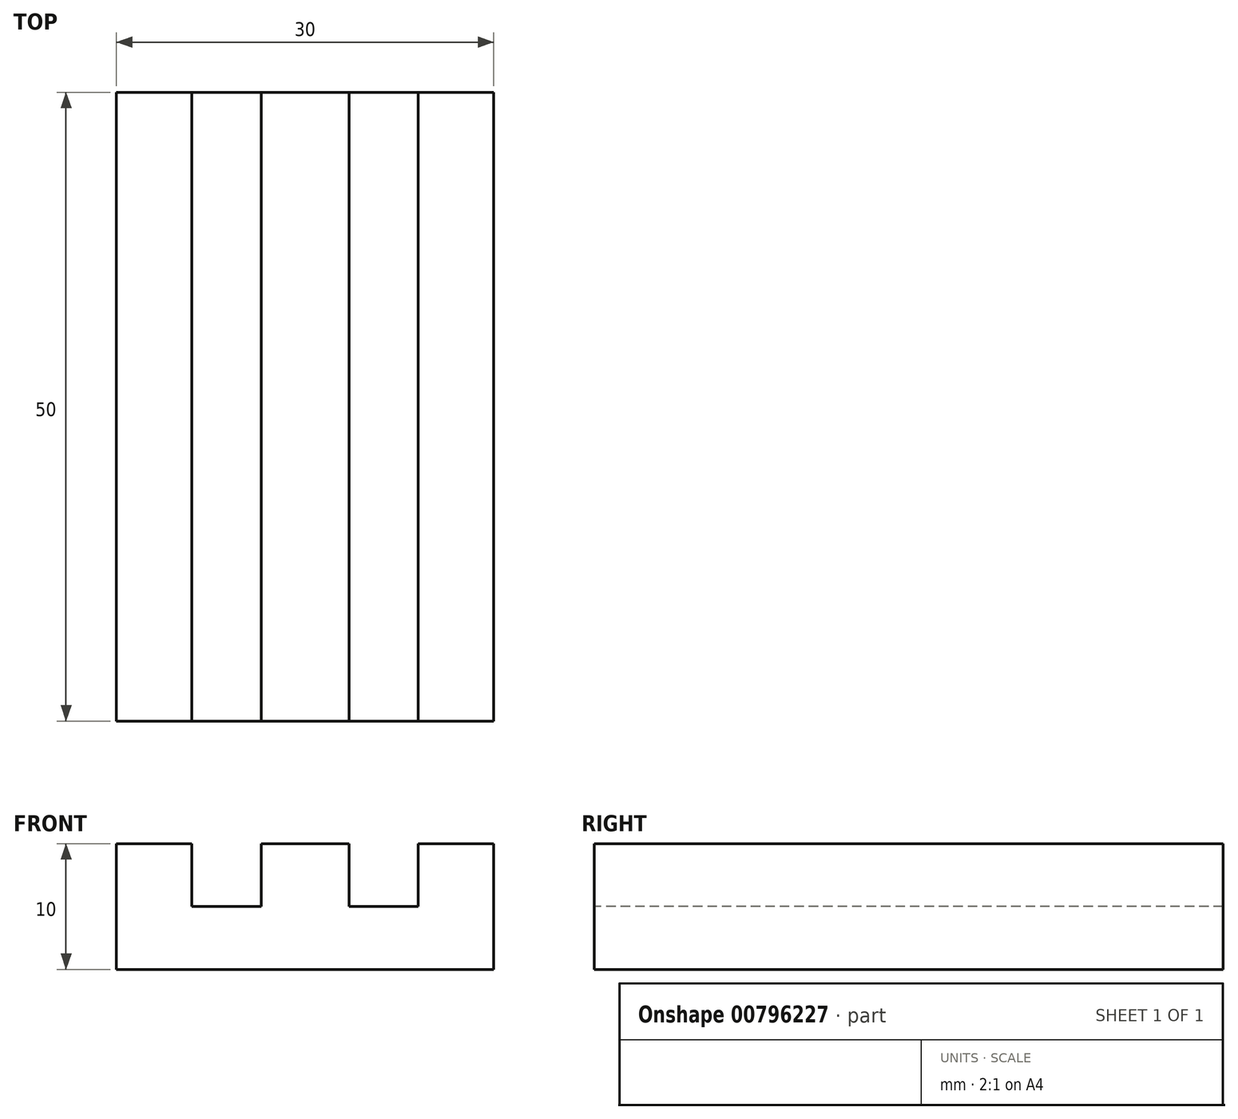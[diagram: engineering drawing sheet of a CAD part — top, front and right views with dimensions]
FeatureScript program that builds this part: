
annotation { "Feature Type Name" : "Feature", "Feature Type Description" : "" }
export const myFeature = defineFeature(function(context is Context, id is Id, definition is map)
    precondition{}
    {
        {
            var Q0;
            Q0=qCreatedBy(makeId("Top.planeOp"),FACE);
            var sketch = newSketch(context, id + "F0", { "sketchPlane" : qUnion([Q0])});
            skLineSegment(sketch, "E0", {"start": v(0, 0) * mm, "end": v(30, 0) * mm});
            skLineSegment(sketch, "E1", {"start": v(30, 0) * mm, "end": v(30, 50) * mm});
            skLineSegment(sketch, "E2", {"start": v(30, 50) * mm, "end": v(0, 50) * mm});
            skLineSegment(sketch, "E3", {"start": v(0, 50) * mm, "end": v(0, 0) * mm});
            skSolve(sketch);
        }
        {
            var Q0;
            Q0 = qSketchRegion(id + "F0", true);
            extrude(context, id + "F1", {"entities" : qUnion([Q0]), "depth" : 5 * mm, "offsetDistance" : 25 * mm});
        }
        {
            var Q0;
            Q0=makeQuery(id+"F1.opExtrude","CAP_FACE",FACE,{"disambiguationData":[OSD([sQuery(id+"F0.wireOp",EDGE,"E0"),sQuery(id+"F0.wireOp",EDGE,"E1"),sQuery(id+"F0.wireOp",EDGE,"E2"),sQuery(id+"F0.wireOp",EDGE,"E3")])],"isStart":false});
            var sketch = newSketch(context, id + "F2", { "sketchPlane" : qUnion([Q0])});
            skLineSegment(sketch, "E4", {"start": v(6, 0) * mm, "end": v(6, 50) * mm});
            skLineSegment(sketch, "E5", {"start": v(11.5, 50) * mm, "end": v(11.5, 0) * mm});
            skLineSegment(sketch, "E6", {"start": v(6, 50) * mm, "end": v(0, 50) * mm});
            skLineSegment(sketch, "E7", {"start": v(0, 50) * mm, "end": v(0, 0) * mm});
            skLineSegment(sketch, "E8", {"start": v(0, 0) * mm, "end": v(6, 0) * mm});
            skLineSegment(sketch, "E9", {"start": v(11.5, 0) * mm, "end": v(18.5, 0) * mm});
            skLineSegment(sketch, "E10", {"start": v(18.5, 0) * mm, "end": v(18.5, 50) * mm});
            skLineSegment(sketch, "E11", {"start": v(18.5, 50) * mm, "end": v(11.5, 50) * mm});
            skLineSegment(sketch, "E12", {"start": v(24, 50) * mm, "end": v(24, 0) * mm});
            skLineSegment(sketch, "E13", {"start": v(24, 0) * mm, "end": v(30, 0) * mm});
            skLineSegment(sketch, "E14", {"start": v(30, 0) * mm, "end": v(30, 50) * mm});
            skLineSegment(sketch, "E15", {"start": v(30, 50) * mm, "end": v(24, 50) * mm});
            skSolve(sketch);
        }
        {
            var Q0;
            Q0 = qSketchRegion(id + "F2", true);
            extrude(context, id + "F3", {"entities" : qUnion([Q0]), "operationType" : NewBodyOperationType.ADD, "depth" : 5 * mm, "offsetDistance" : 25 * mm});
        }
    });
